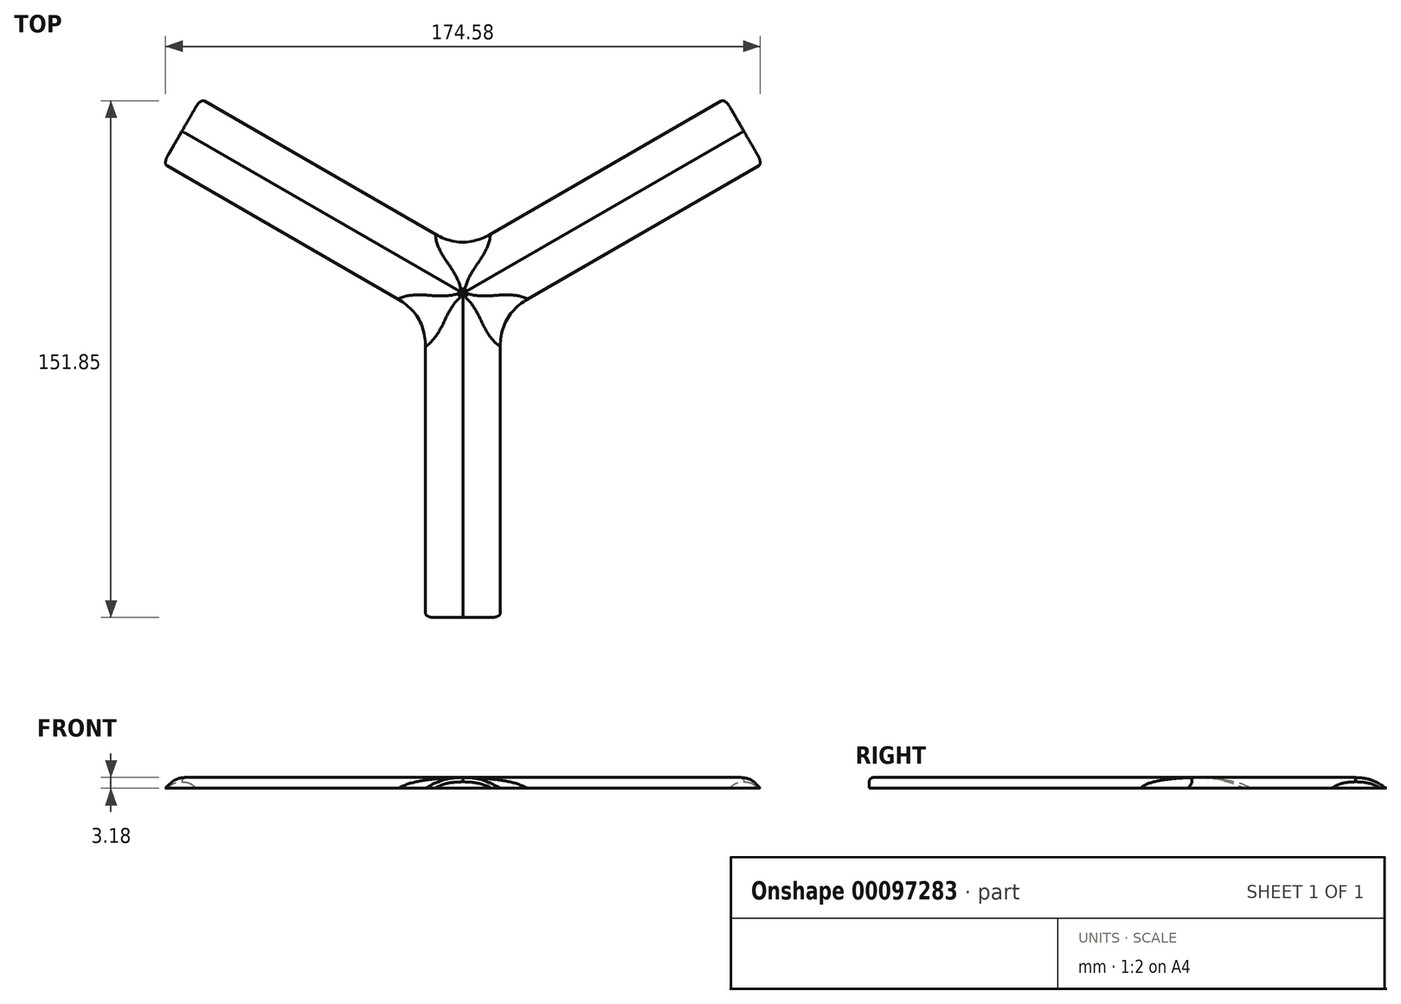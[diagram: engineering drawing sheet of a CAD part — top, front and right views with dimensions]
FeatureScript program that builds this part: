
annotation { "Feature Type Name" : "Feature", "Feature Type Description" : "" }
export const myFeature = defineFeature(function(context is Context, id is Id, definition is map)
    precondition{}
    {
        {
            var Q0;
            Q0=qCreatedBy(makeId("Top.planeOp"),FACE);
            var sketch = newSketch(context, id + "F0", { "sketchPlane" : qUnion([Q0])});
            skCircle(sketch, "E0.cCircle", {"center": v(0, 0) * mm, "radius": 6.35 * mm, "construction": true});
            skLineSegment(sketch, "E0.0", {"start": v(11, -6.35) * mm, "end": v(-11, -6.35) * mm});
            skLineSegment(sketch, "E0.1", {"start": v(-11, -6.35) * mm, "end": v(0, 12.7) * mm});
            skLineSegment(sketch, "E0.2", {"start": v(0, 12.7) * mm, "end": v(11, -6.35) * mm});
            skPoint(sketch, "E0.0.midPoint", {"position": v(0, -6.35) * mm});
            skSolve(sketch);
        }
        {
            var Q0;
            Q0=makeQuery(id+"F0.imprint","IMPRINT",FACE,{"disambiguationData":[TD([[makeQuery(id+"F0.imprint","IMPRINT",EDGE,{"derivedFrom":sQuery(id+"F0.wireOp",EDGE,"E0.0")}),-1.0]])]});
            extrude(context, id + "F1", {"entities" : qUnion([Q0]), "depth" : 3.17 * mm});
        }
        {
            var Q0;
            Q0=makeQuery(id+"F1.opExtrude","SWEPT_FACE",FACE,{"disambiguationData":[OSD([sQuery(id+"F0.wireOp",EDGE,"E0.0")])]});
            var sketch = newSketch(context, id + "F2", { "sketchPlane" : qUnion([Q0])});
            skLineSegment(sketch, "E1", {"start": v(0, 0) * mm, "end": v(0, 3.18) * mm, "construction": true});
            skLineSegment(sketch, "E2", {"start": v(0, 0) * mm, "end": v(-11, 0) * mm});
            skPoint(sketch, "E3.1.internal.snap0", {"position": v(-5.5, 0) * mm});
            skPoint(sketch, "E3.1.internal.snap1", {"position": v(0, 1.59) * mm});
            skLineSegment(sketch, "E4", {"start": v(-11, 0) * mm, "end": v(11, 0) * mm});
            skLineSegment(sketch, "E5", {"start": v(-5.5, 0) * mm, "end": v(-5.5, 2.54) * mm});
            skFitSpline(sketch, "E6", {"points": [v(-11, 0) * mm, v(-5.5, 2.54) * mm, v(0, 3.18) * mm], "startDerivative": vector(10.63, 5.9) * mm, "endDerivative": vector(11.37, 0.4) * mm});
            skFitSpline(sketch, "E7.MirrorCS", {"points": [v(11, 0) * mm, v(5.5, 2.54) * mm, v(0, 3.18) * mm], "startDerivative": vector(-10.63, 5.9) * mm, "endDerivative": vector(-11.37, 0.4) * mm});
            skSolve(sketch);
        }
        {
            var Q0;
            Q0 = qSketchRegion(id + "F2", true);
            extrude(context, id + "F3", {"entities" : qUnion([Q0]), "operationType" : NewBodyOperationType.ADD, "depth" : 88.9 * mm});
        }
        {
            var Q0;
            Q0=makeQuery(id+"F1.opExtrude","SWEPT_FACE",FACE,{"disambiguationData":[OSD([sQuery(id+"F0.wireOp",EDGE,"E0.1")])]});
            var sketch = newSketch(context, id + "F4", { "sketchPlane" : qUnion([Q0])});
            skLineSegment(sketch, "E8", {"start": v(11, 0) * mm, "end": v(-11, 0) * mm});
            skLineSegment(sketch, "E9", {"start": v(-11, 0) * mm, "end": v(0, 0) * mm});
            skLineSegment(sketch, "E10", {"start": v(-5.5, 0) * mm, "end": v(-5.5, 2.54) * mm});
            skFitSpline(sketch, "E11", {"points": [v(-11, 0) * mm, v(-5.5, 2.54) * mm, v(0, 3.18) * mm], "startDerivative": vector(10.63, 5.9) * mm, "endDerivative": vector(11.37, 0.4) * mm});
            skLineSegment(sketch, "E12", {"start": v(0, 0) * mm, "end": v(0, 3.18) * mm});
            skFitSpline(sketch, "E13.MirrorCS", {"points": [v(11, 0) * mm, v(5.5, 2.54) * mm, v(0, 3.18) * mm], "startDerivative": vector(-10.63, 5.9) * mm, "endDerivative": vector(-11.37, 0.4) * mm});
            skSolve(sketch);
        }
        {
            var Q0;
            Q0 = qSketchRegion(id + "F4", true);
            extrude(context, id + "F5", {"entities" : qUnion([Q0]), "operationType" : NewBodyOperationType.ADD, "depth" : 88.9 * mm});
        }
        {
            var Q0;
            Q0=makeQuery(id+"F1.opExtrude","SWEPT_FACE",FACE,{"disambiguationData":[OSD([sQuery(id+"F0.wireOp",EDGE,"E0.2")])]});
            var sketch = newSketch(context, id + "F6", { "sketchPlane" : qUnion([Q0])});
            skLineSegment(sketch, "E14", {"start": v(0, 0) * mm, "end": v(0, 3.18) * mm});
            skLineSegment(sketch, "E15", {"start": v(0, 0) * mm, "end": v(-11, 0) * mm});
            skLineSegment(sketch, "E16", {"start": v(-5.5, 0) * mm, "end": v(-5.5, 2.54) * mm});
            skFitSpline(sketch, "E17", {"points": [v(-11, 0) * mm, v(-5.5, 2.54) * mm, v(0, 3.18) * mm], "startDerivative": vector(10.63, 5.9) * mm, "endDerivative": vector(11.37, 0.4) * mm});
            skFitSpline(sketch, "E18.MirrorCS", {"points": [v(11, 0) * mm, v(5.5, 2.54) * mm, v(0, 3.18) * mm], "startDerivative": vector(-10.63, 5.9) * mm, "endDerivative": vector(-11.37, 0.4) * mm});
            skLineSegment(sketch, "E19", {"start": v(0, 0) * mm, "end": v(11, 0) * mm});
            skSolve(sketch);
        }
        {
            var Q0;
            Q0 = qSketchRegion(id + "F6", true);
            extrude(context, id + "F7", {"entities" : qUnion([Q0]), "operationType" : NewBodyOperationType.ADD, "depth" : 88.9 * mm});
        }
        {
            var Q0;
            Q0=makeQuery(id+"F1.opExtrude","CAP_FACE",FACE,{"disambiguationData":[OSD([sQuery(id+"F0.wireOp",EDGE,"E0.0"),sQuery(id+"F0.wireOp",EDGE,"E0.1"),sQuery(id+"F0.wireOp",EDGE,"E0.2")])],"isStart":false});
            var sketch = newSketch(context, id + "F8", { "sketchPlane" : qUnion([Q0])});
            skLineSegment(sketch, "E20", {"start": v(11, -6.35) * mm, "end": v(-11, -6.35) * mm});
            skLineSegment(sketch, "E21", {"start": v(-11, -6.35) * mm, "end": v(0, 12.7) * mm});
            skLineSegment(sketch, "E22", {"start": v(0, 12.7) * mm, "end": v(11, -6.35) * mm});
            skSolve(sketch);
        }
        {
            var Q0;
            Q0 = qSketchRegion(id + "F8", true);
            extrude(context, id + "F9", {"entities" : qUnion([Q0]), "operationType" : NewBodyOperationType.REMOVE, "endBound" : BoundingType.UP_TO_NEXT, "oppositeDirection" : true, "depth" : 25.4 * mm});
        }
        {
            var Q0;
            Q0=makeQuery(id+"F9.boolean.opBoolean","COPY",FACE,{"derivedFrom":makeQuery(id+"F9.opExtrude","SWEPT_FACE",FACE,{"disambiguationData":[OSD([sQuery(id+"F8.wireOp",EDGE,"E22")])]})});
            extrude(context, id + "F10", {"entities" : qUnion([Q0]), "depth" : 7.62 * mm});
        }
        {
            var Q0;
            Q0=makeQuery(id+"F9.boolean.opBoolean","COPY",FACE,{"derivedFrom":makeQuery(id+"F9.opExtrude","SWEPT_FACE",FACE,{"disambiguationData":[OSD([sQuery(id+"F8.wireOp",EDGE,"E20")])]})});
            extrude(context, id + "F11", {"entities" : qUnion([Q0]), "depth" : 7.62 * mm});
        }
        {
            var Q0;
            Q0=makeQuery(id+"F9.boolean.opBoolean","COPY",FACE,{"derivedFrom":makeQuery(id+"F9.opExtrude","SWEPT_FACE",FACE,{"disambiguationData":[OSD([sQuery(id+"F8.wireOp",EDGE,"E21")])]})});
            extrude(context, id + "F12", {"entities" : qUnion([Q0]), "depth" : 7.62 * mm});
        }
        {
            var Q0;
            Q0=makeQuery(id+"F11.opExtrude","SWEPT_BODY",BODY,{"disambiguationData":[OSD([sQuery(id+"F8.wireOp",EDGE,"E20")])]});
            var Q1;
            Q1=makeQuery(id+"F9.boolean.opBoolean","SPLIT",BODY,{"disambiguationData":[OD(0.0)],"derivedFrom":makeQuery(id+"F1.opExtrude","SWEPT_BODY",BODY,{"disambiguationData":[OSD([sQuery(id+"F0.wireOp",EDGE,"E0.0"),sQuery(id+"F0.wireOp",EDGE,"E0.1"),sQuery(id+"F0.wireOp",EDGE,"E0.2")])]})});
            var Q2;
            Q2=makeQuery(id+"F9.boolean.opBoolean","SPLIT",BODY,{"disambiguationData":[OD(2.0)],"derivedFrom":makeQuery(id+"F1.opExtrude","SWEPT_BODY",BODY,{"disambiguationData":[OSD([sQuery(id+"F0.wireOp",EDGE,"E0.0"),sQuery(id+"F0.wireOp",EDGE,"E0.1"),sQuery(id+"F0.wireOp",EDGE,"E0.2")])]})});
            var Q3;
            Q3=makeQuery(id+"F9.boolean.opBoolean","SPLIT",BODY,{"disambiguationData":[OD(1.0)],"derivedFrom":makeQuery(id+"F1.opExtrude","SWEPT_BODY",BODY,{"disambiguationData":[OSD([sQuery(id+"F0.wireOp",EDGE,"E0.0"),sQuery(id+"F0.wireOp",EDGE,"E0.1"),sQuery(id+"F0.wireOp",EDGE,"E0.2")])]})});
            var Q4;
            Q4=makeQuery(id+"F12.opExtrude","SWEPT_BODY",BODY,{"disambiguationData":[OSD([sQuery(id+"F8.wireOp",EDGE,"E21")])]});
            var Q5;
            Q5=makeQuery(id+"F10.opExtrude","SWEPT_BODY",BODY,{"disambiguationData":[OSD([sQuery(id+"F8.wireOp",EDGE,"E22")])]});
            booleanBodies(context, id + "F13", {"operationType" : BooleanOperationType.UNION, "tools" : qUnion([Q0, Q1, Q2, Q3, Q4, Q5])});
        }
        {
            var Q0;
            Q0=makeQuery(id+"F13.opBoolean","INTERSECT",EDGE,{"derivedFrom":[makeQuery(id+"F11.opExtrude","SWEPT_FACE",FACE,{"disambiguationData":[OSD([sQuery(id+"F2.wireOp",EDGE,"E6")])]}),makeQuery(id+"F12.opExtrude","SWEPT_FACE",FACE,{"disambiguationData":[OSD([sQuery(id+"F4.wireOp",EDGE,"E13.MirrorCS")])]})]});
            var Q1;
            Q1=makeQuery(id+"F13.opBoolean","INTERSECT",EDGE,{"derivedFrom":[makeQuery(id+"F10.opExtrude","SWEPT_FACE",FACE,{"disambiguationData":[OSD([sQuery(id+"F6.wireOp",EDGE,"E18.MirrorCS")])]}),makeQuery(id+"F12.opExtrude","SWEPT_FACE",FACE,{"disambiguationData":[OSD([sQuery(id+"F4.wireOp",EDGE,"E11")])]})]});
            var Q2;
            {var subQ0=sQuery(id+"F2.wireOp",EDGE,"E7.MirrorCS");Q2=makeQuery(id+"F13.opBoolean","INTERSECT",EDGE,{"derivedFrom":[makeQuery(id+"F3.opExtrude","SWEPT_FACE",FACE,{"disambiguationData":[OSD([subQ0])]}),makeQuery(id+"F10.opExtrude","SWEPT_FACE",FACE,{"disambiguationData":[OSD([sQuery(id+"F6.wireOp",EDGE,"E17")])]}),makeQuery(id+"F11.opExtrude","SWEPT_FACE",FACE,{"disambiguationData":[OSD([subQ0])]})]});}
            fillet(context, id + "F14", {"entities" : qUnion([Q0, Q1, Q2]), "radius" : 33.02 * mm, "tangentPropagation" : true, "allowEdgeOverflow" : false});
        }
        {
            var Q0;
            Q0=makeQuery(id+"F7.opExtrude","CAP_EDGE",EDGE,{"disambiguationData":[OSD([sQuery(id+"F6.wireOp",EDGE,"E18.MirrorCS")])],"isStart":false});
            var Q1;
            Q1=makeQuery(id+"F7.opExtrude","CAP_EDGE",EDGE,{"disambiguationData":[OSD([sQuery(id+"F6.wireOp",EDGE,"E17")])],"isStart":false});
            var Q2;
            Q2=makeQuery(id+"F5.opExtrude","CAP_EDGE",EDGE,{"disambiguationData":[OSD([sQuery(id+"F4.wireOp",EDGE,"E13.MirrorCS")])],"isStart":false});
            var Q3;
            Q3=makeQuery(id+"F5.opExtrude","CAP_EDGE",EDGE,{"disambiguationData":[OSD([sQuery(id+"F4.wireOp",EDGE,"E11")])],"isStart":false});
            var Q4;
            Q4=makeQuery(id+"F3.opExtrude","CAP_EDGE",EDGE,{"disambiguationData":[OSD([sQuery(id+"F2.wireOp",EDGE,"E7.MirrorCS")])],"isStart":false});
            var Q5;
            Q5=makeQuery(id+"F3.opExtrude","CAP_EDGE",EDGE,{"disambiguationData":[OSD([sQuery(id+"F2.wireOp",EDGE,"E6")])],"isStart":false});
            fillet(context, id + "F15", {"entities" : qUnion([Q0, Q1, Q2, Q3, Q4, Q5]), "radius" : 1.27 * mm, "tangentPropagation" : true, "allowEdgeOverflow" : false});
        }
    });
